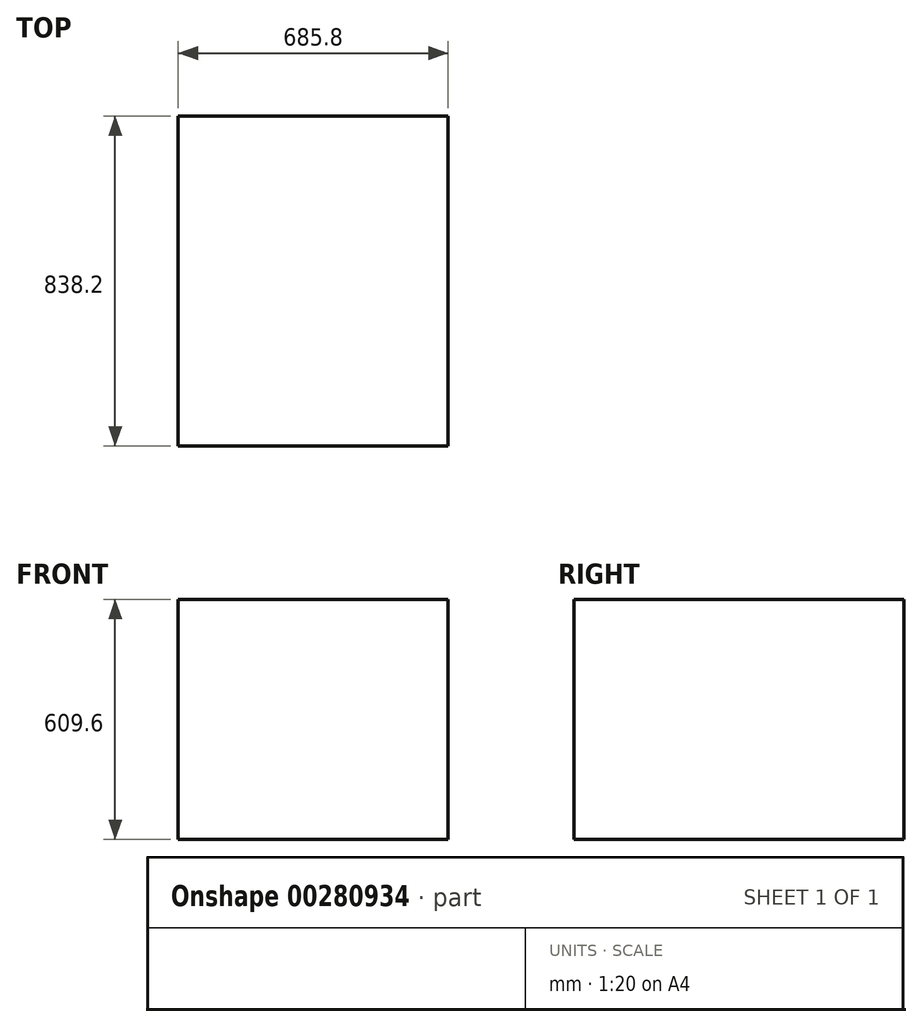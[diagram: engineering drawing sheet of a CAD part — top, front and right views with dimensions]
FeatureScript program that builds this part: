
annotation { "Feature Type Name" : "Feature", "Feature Type Description" : "" }
export const myFeature = defineFeature(function(context is Context, id is Id, definition is map)
    precondition{}
    {
        {
            var Q0;
            Q0=qCreatedBy(makeId("Top.planeOp"),FACE);
            var sketch = newSketch(context, id + "F0", { "sketchPlane" : qUnion([Q0])});
            skLineSegment(sketch, "E0.bottom", {"start": v(0, 0) * mm, "end": v(685.8, 0) * mm});
            skLineSegment(sketch, "E0.top", {"start": v(0, 838.2) * mm, "end": v(685.8, 838.2) * mm});
            skLineSegment(sketch, "E0.left", {"start": v(0, 0) * mm, "end": v(0, 838.2) * mm});
            skLineSegment(sketch, "E0.right", {"start": v(685.8, 0) * mm, "end": v(685.8, 838.2) * mm});
            skSolve(sketch);
        }
        {
            var Q0;
            Q0=makeQuery(id+"F0.imprint","IMPRINT",FACE,{"disambiguationData":[TD([[makeQuery(id+"F0.imprint","IMPRINT",EDGE,{"derivedFrom":sQuery(id+"F0.wireOp",EDGE,"E0.bottom")}),1.0]])]});
            extrude(context, id + "F1", {"entities" : qUnion([Q0]), "depth" : 609.6 * mm});
        }
    });
